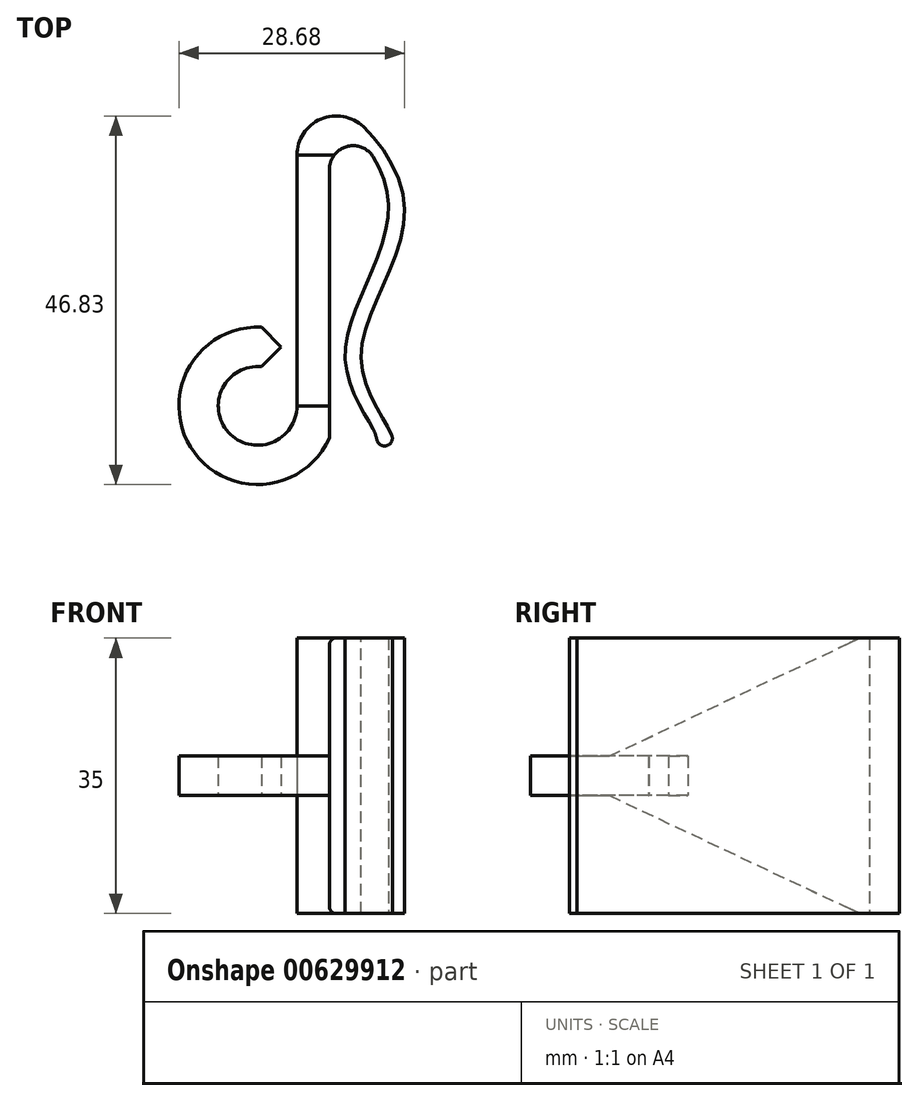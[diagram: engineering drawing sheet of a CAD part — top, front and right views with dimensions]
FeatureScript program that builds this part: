
annotation { "Feature Type Name" : "Feature", "Feature Type Description" : "" }
export const myFeature = defineFeature(function(context is Context, id is Id, definition is map)
    precondition{}
    {
        {
            var Q0;
            Q0=qCreatedBy(makeId("Top.planeOp"),FACE);
            var sketch = newSketch(context, id + "F0", { "sketchPlane" : qUnion([Q0])});
            skCircle(sketch, "E0", {"center": v(0, 0) * mm, "radius": 5 * mm});
            skLineSegment(sketch, "E1", {"start": v(5, -8.66) * mm, "end": v(5, 37.9) * mm});
            skCircle(sketch, "E2", {"center": v(0, 0) * mm, "radius": 10 * mm});
            skLineSegment(sketch, "E3", {"start": v(9.12, -4.1) * mm, "end": v(9.12, 35.9) * mm});
            skFitSpline(sketch, "E4", {"points": [v(9.12, 35.9) * mm, v(16.62, 25.9) * mm, v(11.12, 5.9) * mm, v(15.12, -4.1) * mm], "startDerivative": vector(27.5, 0) * mm, "endDerivative": vector(2.01, -15.72) * mm});
            skFitSpline(sketch, "E5", {"points": [v(9.12, 37.9) * mm, v(18.62, 25.9) * mm, v(13.12, 5.9) * mm, v(17.12, -4.1) * mm], "startDerivative": vector(25.68, 0) * mm, "endDerivative": vector(2.08, -16.24) * mm});
            skLineSegment(sketch, "E6.top", {"start": v(5, 37.9) * mm, "end": v(9.12, 37.9) * mm});
            skLineSegment(sketch, "E7", {"start": v(15.12, -4.1) * mm, "end": v(17.12, -4.1) * mm});
            skLineSegment(sketch, "E8", {"start": v(3, 7.48) * mm, "end": v(0.5, 4.98) * mm});
            skLineSegment(sketch, "E9", {"start": v(3, 7.48) * mm, "end": v(0.5, 9.99) * mm});
            skPoint(sketch, "E10", {"position": v(0.5, 7.48) * mm});
            skCircle(sketch, "E11", {"center": v(16.12, -4.1) * mm, "radius": 1 * mm});
            skSolve(sketch);
        }
        {
            var Q0;
            {var subQ0=sQuery(id+"F0.wireOp",EDGE,"E3");Q0=makeQuery(id+"F0.imprint","IMPRINT",FACE,{"disambiguationData":[TD([[makeQuery(id+"F0.imprint","IMPRINT",EDGE,{"derivedFrom":subQ0}),1.0]])]});}
            var Q1;
            Q1=makeQuery(id+"F0.imprint","IMPRINT",FACE,{"disambiguationData":[TD([[makeQuery(id+"F0.imprint","IMPRINT",EDGE,{"derivedFrom":sQuery(id+"F0.wireOp",EDGE,"E4")}),1.0]])]});
            var Q2;
            {var subQ1=sQuery(id+"F0.wireOp",EDGE,"E7");Q2=makeQuery(id+"F0.imprint","IMPRINT",FACE,{"disambiguationData":[TD([[makeQuery(id+"F0.imprint","IMPRINT",EDGE,{"derivedFrom":subQ1}),1.0]])]});}
            var Q3;
            {var subQ0=sQuery(id+"F0.wireOp",EDGE,"E7");Q3=makeQuery(id+"F0.imprint","IMPRINT",FACE,{"disambiguationData":[TD([[makeQuery(id+"F0.imprint","IMPRINT",EDGE,{"derivedFrom":subQ0}),-1.0]])]});}
            extrude(context, id + "F1", {"entities" : qUnion([Q0, Q1, Q2, Q3]), "depth" : 35 * mm, "offsetDistance" : 25 * mm});
        }
        {
            var Q0;
            {var subQ0=sQuery(id+"F0.wireOp",EDGE,"E8");Q0=makeQuery(id+"F0.imprint","IMPRINT",FACE,{"disambiguationData":[TD([[makeQuery(id+"F0.imprint","IMPRINT",EDGE,{"derivedFrom":subQ0}),-1.0]])]});}
            extrude(context, id + "F2", {"entities" : qUnion([Q0]), "operationType" : NewBodyOperationType.ADD, "depth" : 20 * mm, "offsetDistance" : 25 * mm});
        }
        {
            var Q0;
            {var subQ0=sQuery(id+"F0.wireOp",EDGE,"E8");Q0=makeQuery(id+"F0.imprint","IMPRINT",FACE,{"disambiguationData":[TD([[makeQuery(id+"F0.imprint","IMPRINT",EDGE,{"derivedFrom":subQ0}),-1.0]])]});}
            extrude(context, id + "F3", {"entities" : qUnion([Q0]), "operationType" : NewBodyOperationType.REMOVE, "oppositeDirection" : true, "depth" : -15 * mm, "offsetDistance" : 25 * mm});
        }
        {
            var Q0;
            Q0=makeQuery(id+"F1.opExtrude","SWEPT_EDGE",EDGE,{"disambiguationData":[OSD([sQuery(id+"F0.wireOp",EDGE,"E5"),sQuery(id+"F0.wireOp",EDGE,"E6.top")])]});
            var Q1;
            Q1=makeQuery(id+"F1.opExtrude","SWEPT_EDGE",EDGE,{"disambiguationData":[OSD([sQuery(id+"F0.wireOp",EDGE,"E0"),sQuery(id+"F0.wireOp",EDGE,"E8")])]});
            var Q2;
            Q2=makeQuery(id+"F1.opExtrude","SWEPT_EDGE",EDGE,{"disambiguationData":[OSD([sQuery(id+"F0.wireOp",EDGE,"E3"),sQuery(id+"F0.wireOp",EDGE,"E4")])]});
            fillet(context, id + "F4", {"entities" : qUnion([Q0, Q1, Q2]), "radius" : 3 * mm, "tangentPropagation" : true, "allowEdgeOverflow" : false});
        }
        {
            var Q0;
            Q0=makeQuery(id+"F1.opExtrude","SWEPT_EDGE",EDGE,{"disambiguationData":[OSD([sQuery(id+"F0.wireOp",EDGE,"E1"),sQuery(id+"F0.wireOp",EDGE,"E6.top")])]});
            var Q1;
            Q1=makeQuery(id+"F1.opExtrude","SWEPT_EDGE",EDGE,{"disambiguationData":[OSD([sQuery(id+"F0.wireOp",EDGE,"E4"),sQuery(id+"F0.wireOp",EDGE,"E7"),sQuery(id+"F0.wireOp",EDGE,"E11")])]});
            fillet(context, id + "F5", {"entities" : qUnion([Q0, Q1]), "radius" : 5 * mm, "tangentPropagation" : true, "allowEdgeOverflow" : false});
        }
        {
            var Q0;
            {var subQ0=sQuery(id+"F0.wireOp",EDGE,"E1");Q0=makeQuery(id+"F3.boolean.opBoolean","MERGE",FACE,{"derivedFrom":[makeQuery(id+"F1.opExtrude","SWEPT_FACE",FACE,{"disambiguationData":[OSD([subQ0])]}),makeQuery(id+"F3.opExtrude","SWEPT_FACE",FACE,{"disambiguationData":[OSD([subQ0])]})]});}
            var sketch = newSketch(context, id + "F6", { "sketchPlane" : qUnion([Q0])});
            skLineSegment(sketch, "E12.bottom", {"start": v(8.66, 0) * mm, "end": v(0, 0) * mm});
            skLineSegment(sketch, "E12.top", {"start": v(8.66, 15) * mm, "end": v(0, 15) * mm});
            skLineSegment(sketch, "E12.left", {"start": v(8.66, 0) * mm, "end": v(8.66, 15) * mm});
            skLineSegment(sketch, "E12.right", {"start": v(0, 0) * mm, "end": v(0, 15) * mm});
            skLineSegment(sketch, "E13.bottom", {"start": v(8.66, 35) * mm, "end": v(0, 35) * mm});
            skLineSegment(sketch, "E13.top", {"start": v(8.66, 20) * mm, "end": v(0, 20) * mm});
            skLineSegment(sketch, "E13.left", {"start": v(8.66, 35) * mm, "end": v(8.66, 20) * mm});
            skLineSegment(sketch, "E13.right", {"start": v(0, 35) * mm, "end": v(0, 20) * mm});
            skLineSegment(sketch, "E14", {"start": v(0, 20) * mm, "end": v(-31.83, 35) * mm});
            skLineSegment(sketch, "E15", {"start": v(-31.83, 35) * mm, "end": v(0, 35) * mm});
            skLineSegment(sketch, "E16", {"start": v(0, 15) * mm, "end": v(-31.83, 0) * mm});
            skLineSegment(sketch, "E17", {"start": v(-31.83, 0) * mm, "end": v(0, 0) * mm});
            skSolve(sketch);
        }
        {
            var Q0;
            Q0=makeQuery(id+"F6.imprint","IMPRINT",FACE,{"disambiguationData":[TD([[makeQuery(id+"F6.imprint","IMPRINT",EDGE,{"derivedFrom":sQuery(id+"F6.wireOp",EDGE,"E13.right")}),-1.0]])]});
            var Q1;
            Q1=makeQuery(id+"F6.imprint","IMPRINT",FACE,{"disambiguationData":[TD([[makeQuery(id+"F6.imprint","IMPRINT",EDGE,{"derivedFrom":sQuery(id+"F6.wireOp",EDGE,"E13.bottom")}),1.0]])]});
            var Q2;
            Q2=makeQuery(id+"F6.imprint","IMPRINT",FACE,{"disambiguationData":[TD([[makeQuery(id+"F6.imprint","IMPRINT",EDGE,{"derivedFrom":sQuery(id+"F6.wireOp",EDGE,"E12.bottom")}),-1.0]])]});
            var Q3;
            Q3=makeQuery(id+"F6.imprint","IMPRINT",FACE,{"disambiguationData":[TD([[makeQuery(id+"F6.imprint","IMPRINT",EDGE,{"derivedFrom":sQuery(id+"F6.wireOp",EDGE,"E12.right")}),1.0]])]});
            extrude(context, id + "F7", {"entities" : qUnion([Q0, Q1, Q2, Q3]), "operationType" : NewBodyOperationType.REMOVE, "oppositeDirection" : true, "depth" : 5 * mm, "offsetDistance" : 25 * mm});
        }
    });
